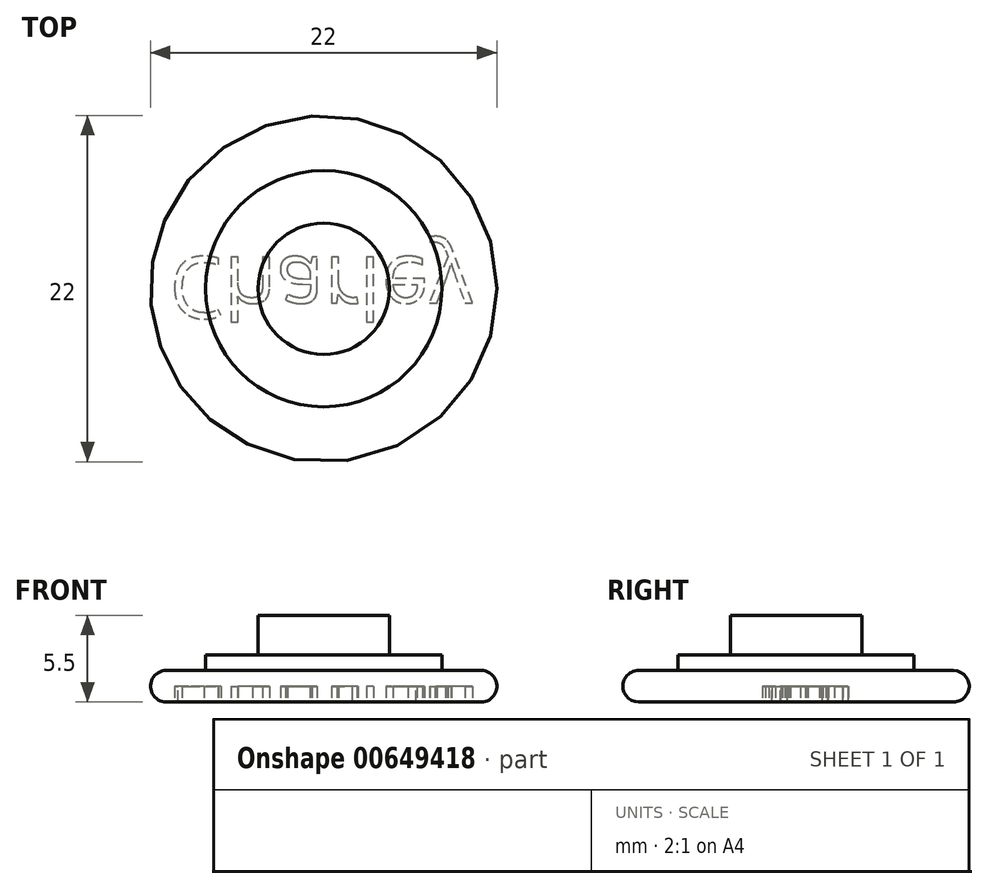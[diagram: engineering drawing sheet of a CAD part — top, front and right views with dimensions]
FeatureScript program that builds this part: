
annotation { "Feature Type Name" : "Feature", "Feature Type Description" : "" }
export const myFeature = defineFeature(function(context is Context, id is Id, definition is map)
    precondition{}
    {
        {
            var Q0;
            Q0=qCreatedBy(makeId("Top.planeOp"),FACE);
            var sketch = newSketch(context, id + "F0", { "sketchPlane" : qUnion([Q0])});
            skCircle(sketch, "E0", {"center": v(0, 0) * mm, "radius": 11 * mm});
            skCircle(sketch, "E1", {"center": v(0, 0) * mm, "radius": 7.5 * mm});
            skCircle(sketch, "E2", {"center": v(0, 0) * mm, "radius": 4.17 * mm});
            skSolve(sketch);
        }
        {
            var Q0;
            Q0=makeQuery(id+"F0.imprint","IMPRINT",FACE,{"disambiguationData":[TD([[makeQuery(id+"F0.imprint","IMPRINT",EDGE,{"derivedFrom":sQuery(id+"F0.wireOp",EDGE,"E0")}),1.0]])]});
            extrude(context, id + "F1", {"entities" : qUnion([Q0]), "depth" : 2 * mm, "offsetDistance" : 25 * mm});
        }
        {
            var Q0;
            Q0=makeQuery(id+"F0.imprint","IMPRINT",FACE,{"disambiguationData":[TD([[makeQuery(id+"F0.imprint","IMPRINT",EDGE,{"derivedFrom":sQuery(id+"F0.wireOp",EDGE,"E1")}),1.0]])]});
            extrude(context, id + "F2", {"entities" : qUnion([Q0]), "operationType" : NewBodyOperationType.ADD, "depth" : 3 * mm, "offsetDistance" : 25 * mm});
        }
        {
            var Q0;
            Q0=makeQuery(id+"F0.imprint","IMPRINT",FACE,{"disambiguationData":[TD([[makeQuery(id+"F0.imprint","IMPRINT",EDGE,{"derivedFrom":sQuery(id+"F0.wireOp",EDGE,"E2")}),1.0]])]});
            extrude(context, id + "F3", {"entities" : qUnion([Q0]), "operationType" : NewBodyOperationType.ADD, "depth" : 5.5 * mm, "offsetDistance" : 25 * mm});
        }
        {
            var Q0;
            Q0=makeQuery(id+"F1.opExtrude","CAP_EDGE",EDGE,{"disambiguationData":[OSD([sQuery(id+"F0.wireOp",EDGE,"E0")])],"isStart":false});
            var Q1;
            Q1=makeQuery(id+"F1.opExtrude","CAP_EDGE",EDGE,{"disambiguationData":[OSD([sQuery(id+"F0.wireOp",EDGE,"E0")])],"isStart":true});
            fillet(context, id + "F4", {"entities" : qUnion([Q0, Q1]), "radius" : 1 * mm, "tangentPropagation" : true, "allowEdgeOverflow" : false});
        }
        {
            var Q0;
            {var subQ0=sQuery(id+"F0.wireOp",EDGE,"E2");var subQ1=sQuery(id+"F0.wireOp",EDGE,"E1");Q0=makeQuery(id+"F3.boolean.opBoolean","MERGE",FACE,{"derivedFrom":[makeQuery(id+"F2.boolean.opBoolean","MERGE",FACE,{"derivedFrom":[makeQuery(id+"F1.opExtrude","CAP_FACE",FACE,{"disambiguationData":[OSD([sQuery(id+"F0.wireOp",EDGE,"E0"),subQ1])],"isStart":true}),makeQuery(id+"F2.opExtrude","CAP_FACE",FACE,{"disambiguationData":[OSD([subQ1,subQ0])],"isStart":true})]}),makeQuery(id+"F3.opExtrude","CAP_FACE",FACE,{"disambiguationData":[OSD([subQ0])],"isStart":true})]});}
            var sketch = newSketch(context, id + "F5", { "sketchPlane" : qUnion([Q0])});
            skText(sketch, "E3", { "text": "Charley", "fontName": "OpenSans-Regular.ttf"});
            const initialGuessF5  = {"E3": [-0.0098, -0.00202, 1, 0, 0.00393]};
            skSetInitialGuess(sketch, initialGuessF5);
            skSolve(sketch);
        }
        {
            var Q0;
            Q0 = qSketchRegion(id + "F5", true);
            extrude(context, id + "F6", {"entities" : qUnion([Q0]), "operationType" : NewBodyOperationType.REMOVE, "oppositeDirection" : true, "depth" : 1 * mm, "offsetDistance" : 25 * mm});
        }
    });
